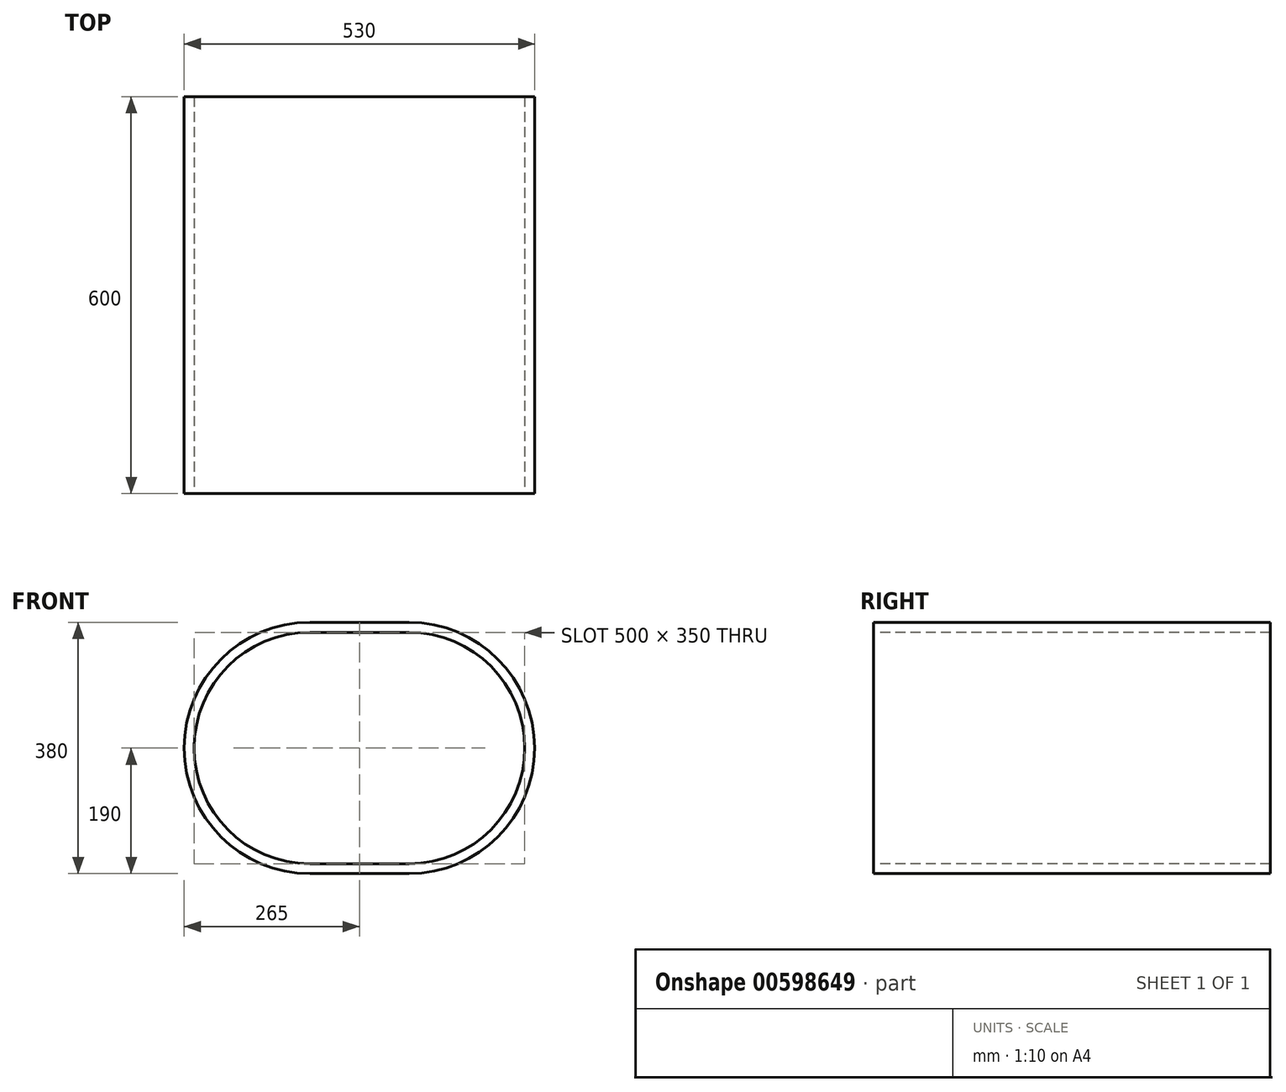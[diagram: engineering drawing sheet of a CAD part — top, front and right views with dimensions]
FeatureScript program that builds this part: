
annotation { "Feature Type Name" : "Feature", "Feature Type Description" : "" }
export const myFeature = defineFeature(function(context is Context, id is Id, definition is map)
    precondition{}
    {
        {
            var Q0;
            Q0=qCreatedBy(makeId("Front.planeOp"),FACE);
            var sketch = newSketch(context, id + "F0", { "sketchPlane" : qUnion([Q0])});
            skPoint(sketch, "E0.middle", {"position": v(0, 0) * mm});
            skLineSegment(sketch, "E1", {"start": v(-75, 0) * mm, "end": v(75, 0) * mm});
            skPoint(sketch, "E0.top.end.orphan", {"position": v(-75, -55.71) * mm});
            skPoint(sketch, "E0.top.start.orphan", {"position": v(75, -55.71) * mm});
            skPoint(sketch, "E0.bottom.end.orphan", {"position": v(-75, 55.71) * mm});
            skPoint(sketch, "E0.left.start.orphan", {"position": v(75, 55.71) * mm});
            skArc(sketch, "E2.0.startCap", {"start": v(-75, -175) * mm, "mid": v(-250, 0) * mm, "end": v(-75, 175) * mm});
            skArc(sketch, "E2.0.endCap", {"start": v(75, 175) * mm, "mid": v(250, 0) * mm, "end": v(75, -175) * mm});
            skLineSegment(sketch, "E2.0.left", {"start": v(-75, 175) * mm, "end": v(75, 175) * mm});
            skLineSegment(sketch, "E2.0.right", {"start": v(-75, -175) * mm, "end": v(75, -175) * mm});
            skSolve(sketch);
        }
        {
            var Q0;
            Q0 = qSketchRegion(id + "F0", true);
            var sketch = newSketch(context, id + "F1", { "sketchPlane" : qUnion([Q0])});
            skLineSegment(sketch, "E3.0", {"start": v(-75, 190) * mm, "end": v(75, 190) * mm});
            skArc(sketch, "E3.1", {"start": v(-75, -190) * mm, "mid": v(-265, 0) * mm, "end": v(-75, 190) * mm});
            skLineSegment(sketch, "E3.2", {"start": v(-75, -190) * mm, "end": v(75, -190) * mm});
            skArc(sketch, "E3.3", {"start": v(75, 190) * mm, "mid": v(265, 0) * mm, "end": v(75, -190) * mm});
            skSolve(sketch);
        }
        {
            var Q0;
            Q0=makeQuery(id+"F1.imprint","IMPRINT",FACE,{"disambiguationData":[TD([[makeQuery(id+"F1.imprint","IMPRINT",EDGE,{"derivedFrom":makeQuery(id+"F0.imprint","IMPRINT",EDGE,{"derivedFrom":sQuery(id+"F0.wireOp",EDGE,"E2.0.startCap")})}),-1.0]])]});
            var Q1;
            Q1=makeQuery(id+"F1.imprint","IMPRINT",FACE,{"disambiguationData":[TD([[makeQuery(id+"F1.imprint","IMPRINT",EDGE,{"derivedFrom":sQuery(id+"F1.wireOp",EDGE,"E3.0")}),-1.0]])]});
            var Q2;
            Q2=makeQuery(id+"F0.imprint","IMPRINT",FACE,{"disambiguationData":[TD([[makeQuery(id+"F0.imprint","IMPRINT",EDGE,{"derivedFrom":sQuery(id+"F0.wireOp",EDGE,"E2.0.startCap")}),-1.0]])]});
            extrude(context, id + "F2", {"entities" : qUnion([Q0, Q1, Q2]), "oppositeDirection" : true, "depth" : 600 * mm, "offsetDistance" : 25 * mm});
        }
    });
